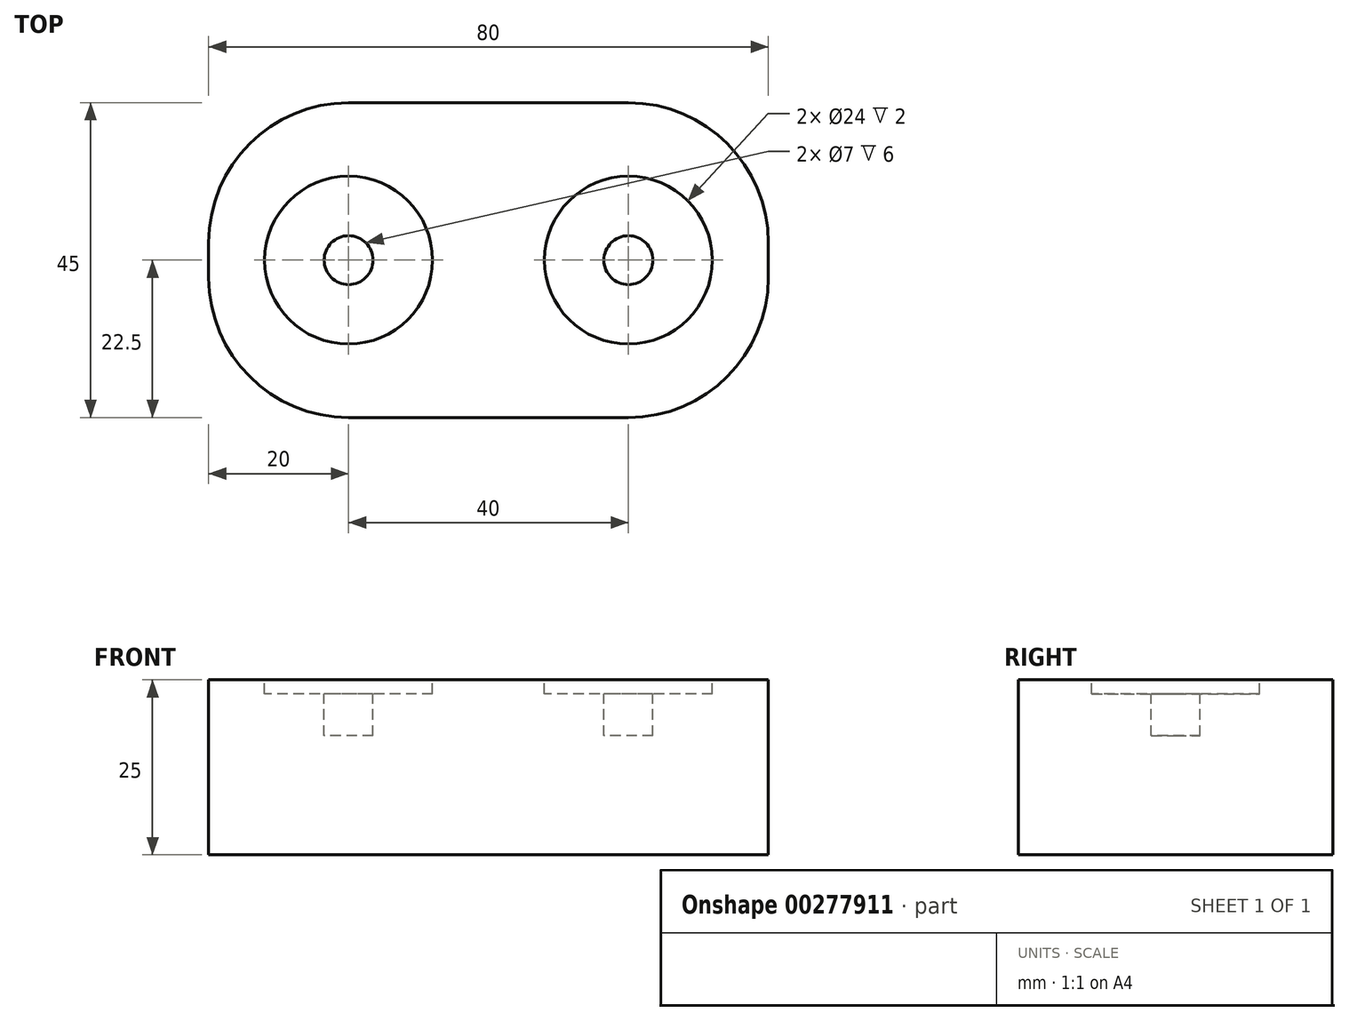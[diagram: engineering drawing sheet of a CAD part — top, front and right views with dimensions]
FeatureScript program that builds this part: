
annotation { "Feature Type Name" : "Feature", "Feature Type Description" : "" }
export const myFeature = defineFeature(function(context is Context, id is Id, definition is map)
    precondition{}
    {
        {
            var Q0;
            Q0=qCreatedBy(makeId("Top.planeOp"),FACE);
            var sketch = newSketch(context, id + "F0", { "sketchPlane" : qUnion([Q0])});
            skLineSegment(sketch, "E0.bottom", {"start": v(40, 22.5) * mm, "end": v(-40, 22.5) * mm});
            skLineSegment(sketch, "E0.top", {"start": v(40, -22.5) * mm, "end": v(-40, -22.5) * mm});
            skLineSegment(sketch, "E0.left", {"start": v(40, 22.5) * mm, "end": v(40, -22.5) * mm});
            skLineSegment(sketch, "E0.right", {"start": v(-40, 22.5) * mm, "end": v(-40, -22.5) * mm});
            skPoint(sketch, "E0.middle", {"position": v(0, 0) * mm});
            skSolve(sketch);
        }
        {
            var Q0;
            Q0 = qSketchRegion(id + "F0", true);
            extrude(context, id + "F1", {"entities" : qUnion([Q0]), "depth" : 25 * mm});
        }
        {
            var Q0;
            Q0=makeQuery(id+"F1.opExtrude","CAP_FACE",FACE,{"disambiguationData":[OSD([sQuery(id+"F0.wireOp",EDGE,"E0.bottom"),sQuery(id+"F0.wireOp",EDGE,"E0.top"),sQuery(id+"F0.wireOp",EDGE,"E0.left"),sQuery(id+"F0.wireOp",EDGE,"E0.right")])],"isStart":false});
            var sketch = newSketch(context, id + "F2", { "sketchPlane" : qUnion([Q0])});
            skCircle(sketch, "E1", {"center": v(-20, 0) * mm, "radius": 12 * mm});
            skLineSegment(sketch, "E2", {"start": v(0, 0) * mm, "end": v(-49.33, 0) * mm, "construction": true});
            skLineSegment(sketch, "E3", {"start": v(0, 0) * mm, "end": v(0, 11.86) * mm, "construction": true});
            skCircle(sketch, "E4.MirrorC", {"center": v(20, 0) * mm, "radius": 12 * mm});
            skSolve(sketch);
        }
        {
            var Q0;
            Q0 = qSketchRegion(id + "F2", true);
            extrude(context, id + "F3", {"entities" : qUnion([Q0]), "operationType" : NewBodyOperationType.REMOVE, "oppositeDirection" : true, "depth" : 2 * mm});
        }
        {
            var Q0;
            Q0=makeQuery(id+"F3.boolean.opBoolean","COPY",FACE,{"derivedFrom":makeQuery(id+"F3.opExtrude","CAP_FACE",FACE,{"disambiguationData":[OSD([sQuery(id+"F2.wireOp",EDGE,"E1")])],"isStart":false})});
            var sketch = newSketch(context, id + "F4", { "sketchPlane" : qUnion([Q0])});
            skCircle(sketch, "E5", {"center": v(-20, 0) * mm, "radius": 3.5 * mm});
            skLineSegment(sketch, "E6", {"start": v(0, 0) * mm, "end": v(0, 7.3) * mm, "construction": true});
            skCircle(sketch, "E7.MirrorC", {"center": v(20, 0) * mm, "radius": 3.5 * mm});
            skSolve(sketch);
        }
        {
            var Q0;
            Q0 = qSketchRegion(id + "F4", true);
            extrude(context, id + "F5", {"entities" : qUnion([Q0]), "operationType" : NewBodyOperationType.REMOVE, "oppositeDirection" : true, "depth" : 6 * mm});
        }
        {
            var Q0;
            Q0=makeQuery(id+"F1.opExtrude","SWEPT_EDGE",EDGE,{"disambiguationData":[OSD([sQuery(id+"F0.wireOp",EDGE,"E0.top"),sQuery(id+"F0.wireOp",EDGE,"E0.right")])]});
            var Q1;
            Q1=makeQuery(id+"F1.opExtrude","SWEPT_EDGE",EDGE,{"disambiguationData":[OSD([sQuery(id+"F0.wireOp",EDGE,"E0.bottom"),sQuery(id+"F0.wireOp",EDGE,"E0.right")])]});
            var Q2;
            Q2=makeQuery(id+"F1.opExtrude","SWEPT_EDGE",EDGE,{"disambiguationData":[OSD([sQuery(id+"F0.wireOp",EDGE,"E0.top"),sQuery(id+"F0.wireOp",EDGE,"E0.left")])]});
            var Q3;
            Q3=makeQuery(id+"F1.opExtrude","SWEPT_EDGE",EDGE,{"disambiguationData":[OSD([sQuery(id+"F0.wireOp",EDGE,"E0.bottom"),sQuery(id+"F0.wireOp",EDGE,"E0.left")])]});
            fillet(context, id + "F6", {"entities" : qUnion([Q0, Q1, Q2, Q3]), "radius" : 20 * mm, "tangentPropagation" : true, "allowEdgeOverflow" : false});
        }
    });
